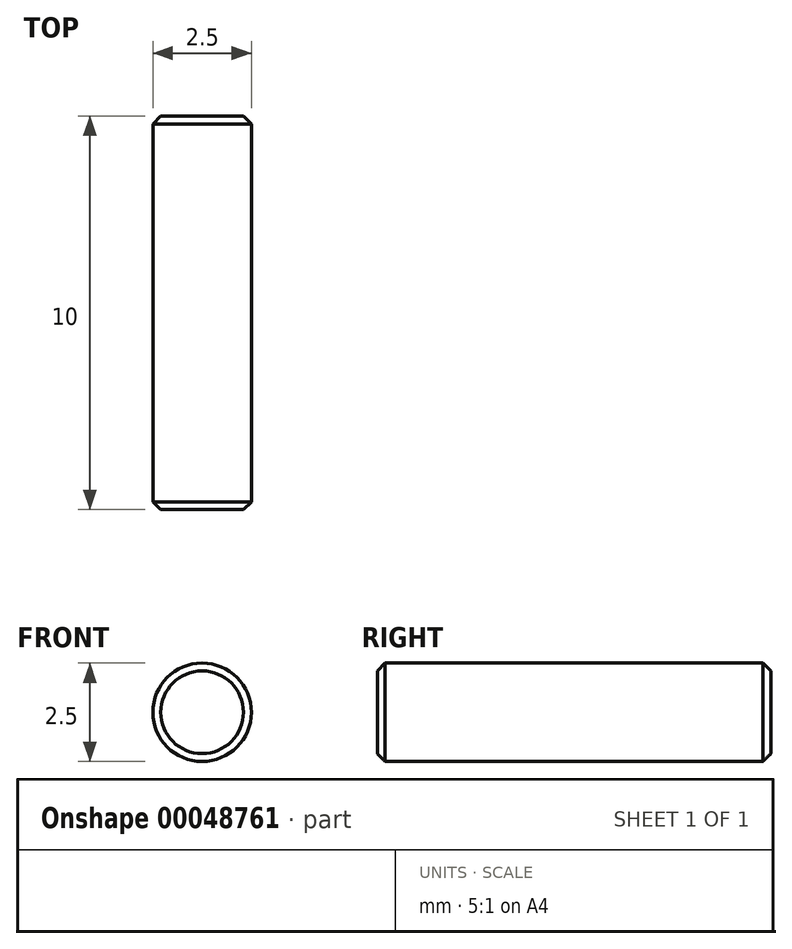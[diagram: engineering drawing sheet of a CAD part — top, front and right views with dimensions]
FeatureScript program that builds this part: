
annotation { "Feature Type Name" : "Feature", "Feature Type Description" : "" }
export const myFeature = defineFeature(function(context is Context, id is Id, definition is map)
    precondition{}
    {
        {
            var Q0;
            Q0=qCreatedBy(makeId("Front.planeOp"),FACE);
            var sketch = newSketch(context, id + "F0", { "sketchPlane" : qUnion([Q0])});
            skCircle(sketch, "E0", {"center": v(0, 0) * mm, "radius": 1.25 * mm});
            skSolve(sketch);
        }
        {
            var Q0;
            Q0=makeQuery(id+"F0.imprint","IMPRINT",FACE,{"disambiguationData":[TD([[makeQuery(id+"F0.imprint","IMPRINT",EDGE,{"derivedFrom":sQuery(id+"F0.wireOp",EDGE,"E0")}),1.0]])]});
            extrude(context, id + "F1", {"entities" : qUnion([Q0]), "depth" : 5 * mm});
        }
        {
            var Q0;
            Q0=makeQuery(id+"F1.opExtrude","CAP_EDGE",EDGE,{"disambiguationData":[OSD([sQuery(id+"F0.wireOp",EDGE,"E0")])],"isStart":false});
            chamfer(context, id + "F2", {"entities" : qUnion([Q0]), "width" : 0.2 * mm, "tangentPropagation" : true});
        }
        {
            var Q0;
            Q0=makeQuery(id+"F1.opExtrude","SWEPT_BODY",BODY,{"disambiguationData":[OSD([sQuery(id+"F0.wireOp",EDGE,"E0")])]});
            var Q1;
            Q1=qCreatedBy(makeId("Front.planeOp"),FACE);
            mirror(context, id + "F3", {"operationType" : NewBodyOperationType.ADD, "entities" : qUnion([Q0]), "mirrorPlane" : qUnion([Q1])});
        }
    });
